# Revit family: Zumtobel PANOS3 R R150
name_source: partatom
category: Lighting Fixtures
revit_build: Autodesk Revit 2018 (Build: 20170223_1515(x64)
units: mm (PartAtom-declared; Revit-internal decimal feet)

## family parameters
Cut with Voids When Loaded = No
Host = Face
Light Source = Yes
OmniClass Number = 23.80.70.11
OmniClass Title = Luminaries for Internal Lighting
Part Type = Normal
Room Calculation Point = No
Round Connector Dimension = Use Diameter
Shared = No

## types (4) — shared parameters
Apparent Load = 8 VA
Assembly Code = D5020200
Body = ZG_Metal_White
Color Filter = 16777215
Cover Diameter = 164 mm
Cutout Diameter = 150 mm
Description = LED ceiling-recessed luminaire
Dimming Lamp Color Temperature Shift = <None>
Emit Shape Visible in Rendering = Yes
Emit from Circle Diameter = 164 mm
Lamp = LED
Manufacturer = Zumtobel Lighting
Reflector = ZG_Metal_White_Self_Illumination
Tilt Angle = -90.00°
URL = http://www.zumtobel.com
Voltage = 230 V
zero-valued in all types: Default Elevation

## per-type parameters (varying)
| type | Clearance Height | Height | Length | Model | Photometric Web File | R150H | R150L | WH | Width |
| PANOS3 R R150H TL | 100 mm  [stored 0.328084 ft] | 94 mm | 150 mm | 60819281 | 60819281_(STD).IES | Yes | No | No | 150 mm |
| PANOS3 R R150H WH | 100 mm  [stored 0.328084 ft] | 94 mm | 164 mm | 60819244 | 60819244_(STD).IES | Yes | No | Yes | 164 mm |
| PANOS3 R R150L TL | 70 mm  [stored 0.229659 ft] | 59 mm | 150 mm | 60819284 | 60819284_(STD).IES | No | Yes | No | 150 mm |
| PANOS3 R R150L WH | 70 mm  [stored 0.229659 ft] | 59 mm | 164 mm | 60819286 | 60819286_(STD).IES | No | Yes | Yes | 164 mm |

note: [stored X ft] marks values corroborated as IEEE doubles in the binary element streams (Revit-internal decimal feet)

## geometry (parser evidence)
native form markers: Sweep x3
no freeform markers — native parametric forms only
